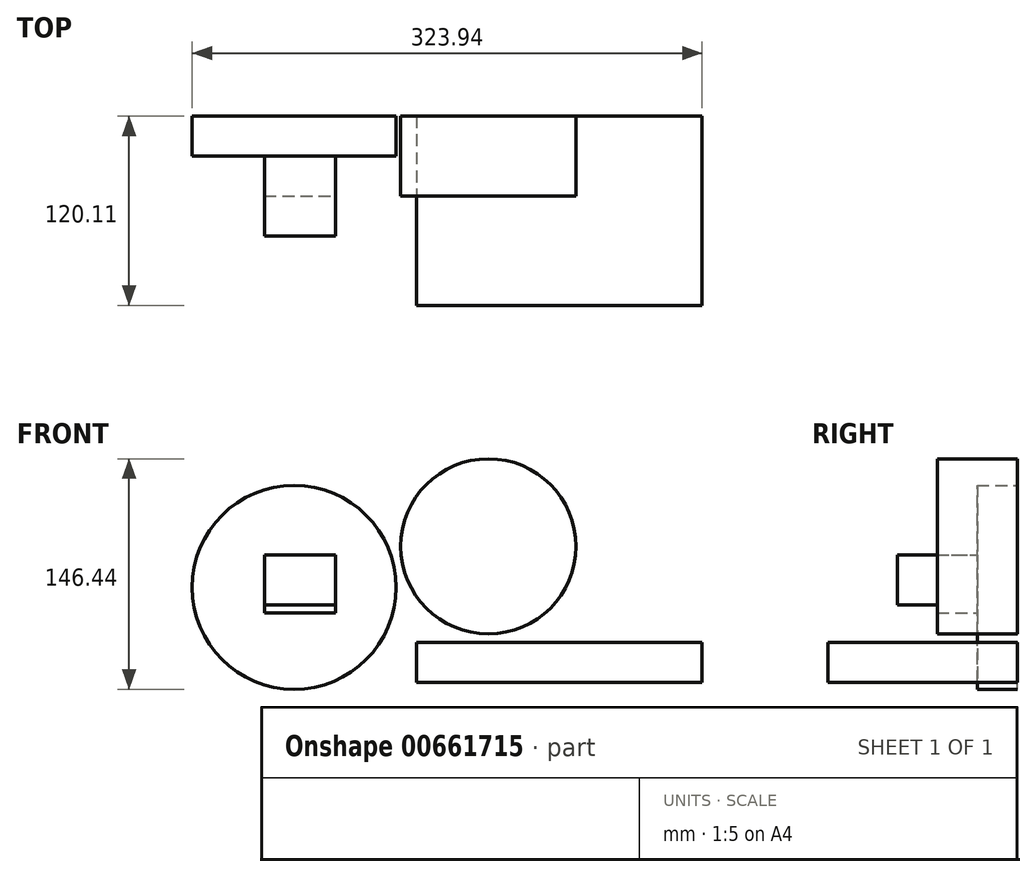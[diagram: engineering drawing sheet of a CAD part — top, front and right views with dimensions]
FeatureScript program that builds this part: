
annotation { "Feature Type Name" : "Feature", "Feature Type Description" : "" }
export const myFeature = defineFeature(function(context is Context, id is Id, definition is map)
    precondition{}
    {
        {
            var Q0;
            Q0=qCreatedBy(makeId("Front.planeOp"),FACE);
            var sketch = newSketch(context, id + "F0", { "sketchPlane" : qUnion([Q0])});
            skCircle(sketch, "E0", {"center": v(-61.68, 60.34) * mm, "radius": 64.78 * mm});
            skSolve(sketch);
        }
        {
            var Q0;
            Q0=makeQuery(id+"F0.imprint","IMPRINT",FACE,{"disambiguationData":[TD([[makeQuery(id+"F0.imprint","IMPRINT",EDGE,{"derivedFrom":sQuery(id+"F0.wireOp",EDGE,"E0")}),1.0]])]});
            extrude(context, id + "F1", {"entities" : qUnion([Q0]), "depth" : 25.4 * mm, "offsetDistance" : 25.4 * mm});
        }
        {
            var Q0;
            Q0=makeQuery(id+"F1.opExtrude","CAP_FACE",FACE,{"disambiguationData":[OSD([sQuery(id+"F0.wireOp",EDGE,"E0")])],"isStart":false});
            var sketch = newSketch(context, id + "F2", { "sketchPlane" : qUnion([Q0])});
            skLineSegment(sketch, "E1.bottom", {"start": v(-80.54, 80.76) * mm, "end": v(-60.78, 80.76) * mm});
            skLineSegment(sketch, "E1.top", {"start": v(-80.54, 43.95) * mm, "end": v(-60.78, 43.95) * mm});
            skLineSegment(sketch, "E1.left", {"start": v(-80.54, 80.76) * mm, "end": v(-80.54, 43.95) * mm});
            skLineSegment(sketch, "E1.right", {"start": v(-60.78, 80.76) * mm, "end": v(-60.78, 43.95) * mm});
            skSolve(sketch);
        }
        {
            var Q0;
            Q0 = qSketchRegion(id + "F2", true);
            extrude(context, id + "F3", {"entities" : qUnion([Q0]), "operationType" : NewBodyOperationType.ADD, "depth" : 25.4 * mm, "offsetDistance" : 25.4 * mm});
        }
        {
            var Q0;
            Q0=makeQuery(id+"F3.opExtrude","SWEPT_FACE",FACE,{"disambiguationData":[OSD([sQuery(id+"F2.wireOp",EDGE,"E1.right")])]});
            extrude(context, id + "F4", {"entities" : qUnion([Q0]), "operationType" : NewBodyOperationType.ADD, "depth" : 25.4 * mm, "offsetDistance" : 25.4 * mm});
        }
        {
            var Q0;
            {var subQ0=sQuery(id+"F2.wireOp",EDGE,"E1.right");Q0=makeQuery(id+"F4.boolean.opBoolean","MERGE",FACE,{"derivedFrom":[makeQuery(id+"F3.opExtrude","CAP_FACE",FACE,{"disambiguationData":[OSD([sQuery(id+"F2.wireOp",EDGE,"E1.bottom"),sQuery(id+"F2.wireOp",EDGE,"E1.top"),sQuery(id+"F2.wireOp",EDGE,"E1.left"),subQ0])],"isStart":false}),makeQuery(id+"F4.opExtrude","SWEPT_FACE",FACE,{"disambiguationData":[OSD([subQ0]),TDD([makeQuery(id+"F3.opExtrude","CAP_EDGE",EDGE,{"disambiguationData":[OSD([subQ0])],"isStart":false})])]})]});}
            var sketch = newSketch(context, id + "F5", { "sketchPlane" : qUnion([Q0])});
            skLineSegment(sketch, "E2.bottom", {"start": v(-80.54, 80.76) * mm, "end": v(-35.38, 80.76) * mm});
            skLineSegment(sketch, "E2.top", {"start": v(-80.54, 49.19) * mm, "end": v(-35.38, 49.19) * mm});
            skLineSegment(sketch, "E2.left", {"start": v(-80.54, 80.76) * mm, "end": v(-80.54, 49.19) * mm});
            skLineSegment(sketch, "E2.right", {"start": v(-35.38, 80.76) * mm, "end": v(-35.38, 49.19) * mm});
            skLineSegment(sketch, "E3.bottom", {"start": v(-35.38, 49.19) * mm, "end": v(-64.08, 49.19) * mm});
            skLineSegment(sketch, "E3.top", {"start": v(-35.38, 43.95) * mm, "end": v(-64.08, 43.95) * mm});
            skLineSegment(sketch, "E3.left", {"start": v(-35.38, 49.19) * mm, "end": v(-35.38, 43.95) * mm});
            skLineSegment(sketch, "E3.right", {"start": v(-64.08, 49.19) * mm, "end": v(-64.08, 43.95) * mm});
            skSolve(sketch);
        }
        {
            var Q0;
            Q0=makeQuery(id+"F5.imprint","IMPRINT",FACE,{"disambiguationData":[TD([[makeQuery(id+"F5.imprint","IMPRINT",EDGE,{"derivedFrom":sQuery(id+"F5.wireOp",EDGE,"E3.bottom")}),1.0]])]});
            var Q1;
            Q1=makeQuery(id+"F5.imprint","IMPRINT",FACE,{"disambiguationData":[TD([[makeQuery(id+"F5.imprint","IMPRINT",EDGE,{"derivedFrom":sQuery(id+"F5.wireOp",EDGE,"E2.bottom")}),-1.0]])]});
            extrude(context, id + "F6", {"entities" : qUnion([Q0, Q1]), "operationType" : NewBodyOperationType.ADD, "depth" : 25.4 * mm, "offsetDistance" : 25.4 * mm});
        }
        {
            var Q0;
            Q0=qCreatedBy(makeId("Top.planeOp"),FACE);
            var sketch = newSketch(context, id + "F7", { "sketchPlane" : qUnion([Q0])});
            skLineSegment(sketch, "E4.bottom", {"start": v(16.19, 0) * mm, "end": v(197.5, 0) * mm});
            skLineSegment(sketch, "E4.top", {"start": v(16.19, -120.11) * mm, "end": v(197.5, -120.11) * mm});
            skLineSegment(sketch, "E4.left", {"start": v(16.19, 0) * mm, "end": v(16.19, -120.11) * mm});
            skLineSegment(sketch, "E4.right", {"start": v(197.5, 0) * mm, "end": v(197.5, -120.11) * mm});
            skSolve(sketch);
        }
        {
            var Q0;
            Q0=makeQuery(id+"F7.imprint","IMPRINT",FACE,{"disambiguationData":[TD([[makeQuery(id+"F7.imprint","IMPRINT",EDGE,{"derivedFrom":sQuery(id+"F7.wireOp",EDGE,"E4.bottom")}),-1.0]])]});
            extrude(context, id + "F8", {"entities" : qUnion([Q0]), "depth" : 25.4 * mm, "offsetDistance" : 25.4 * mm});
        }
        {
            var Q0;
            Q0=qCreatedBy(makeId("Front.planeOp"),FACE);
            var sketch = newSketch(context, id + "F9", { "sketchPlane" : qUnion([Q0])});
            skCircle(sketch, "E5", {"center": v(61.68, 86.36) * mm, "radius": 55.64 * mm});
            skSolve(sketch);
        }
        {
            var Q0;
            Q0=makeQuery(id+"F9.imprint","IMPRINT",FACE,{"disambiguationData":[TD([[makeQuery(id+"F9.imprint","IMPRINT",EDGE,{"derivedFrom":sQuery(id+"F9.wireOp",EDGE,"E5")}),1.0]])]});
            extrude(context, id + "F10", {"entities" : qUnion([Q0]), "depth" : 25.4 * mm, "offsetDistance" : 25.4 * mm});
        }
        {
            var Q0;
            Q0=makeQuery(id+"F10.opExtrude","CAP_FACE",FACE,{"disambiguationData":[OSD([sQuery(id+"F9.wireOp",EDGE,"E5")])],"isStart":false});
            extrude(context, id + "F11", {"entities" : qUnion([Q0]), "operationType" : NewBodyOperationType.ADD, "depth" : 25.4 * mm, "offsetDistance" : 25.4 * mm});
        }
    });
